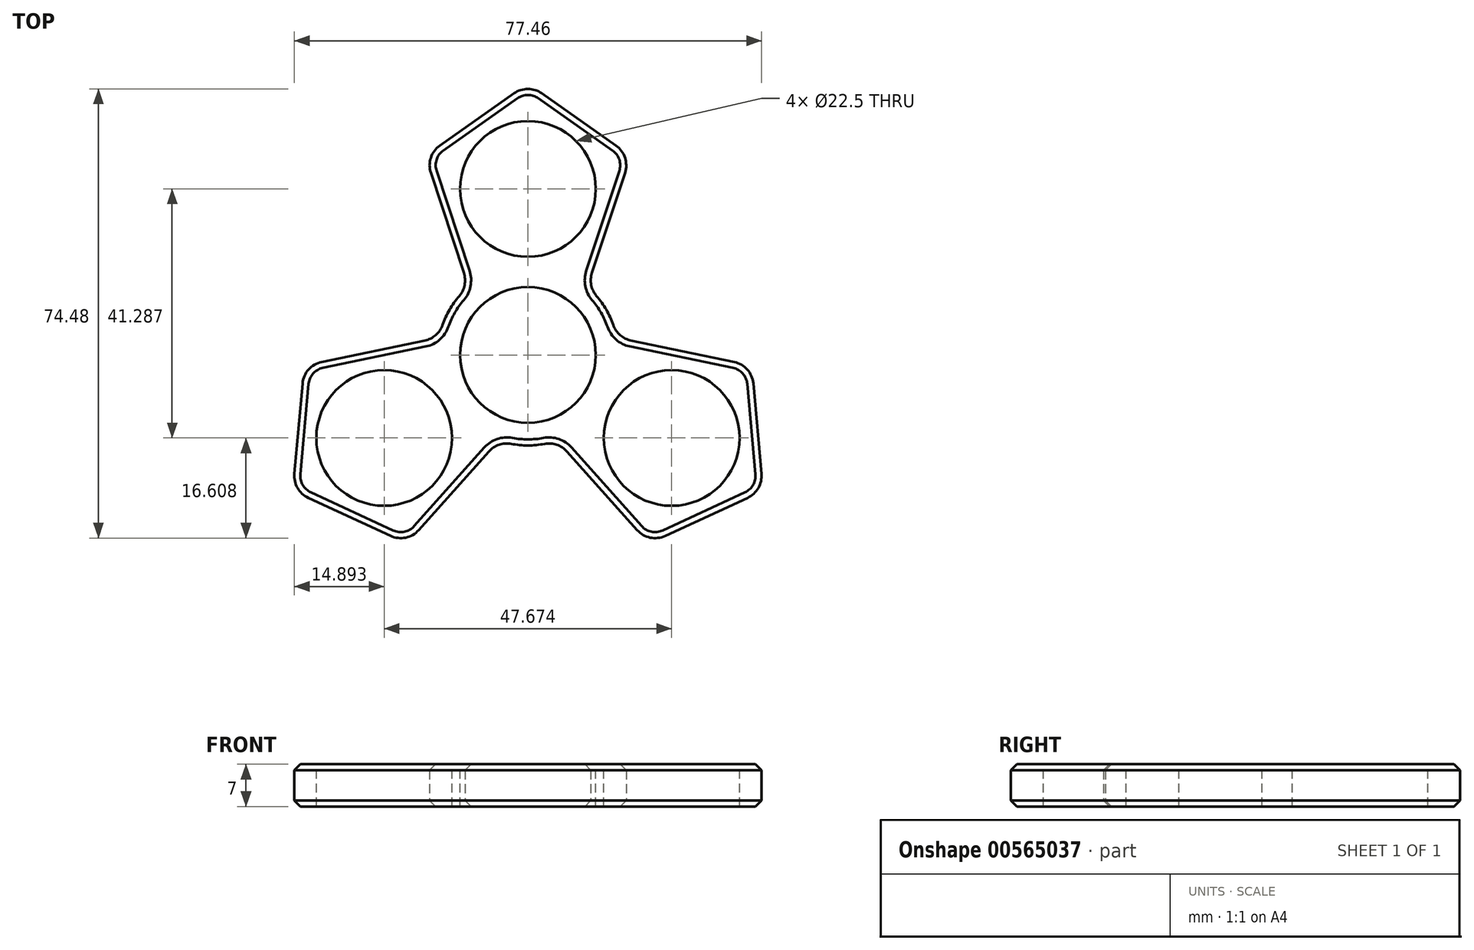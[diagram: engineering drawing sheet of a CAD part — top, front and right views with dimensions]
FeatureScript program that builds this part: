
annotation { "Feature Type Name" : "Feature", "Feature Type Description" : "" }
export const myFeature = defineFeature(function(context is Context, id is Id, definition is map)
    precondition{}
    {
        {
            var Q0;
            Q0=qCreatedBy(makeId("Top.planeOp"),FACE);
            var sketch = newSketch(context, id + "F0", { "sketchPlane" : qUnion([Q0])});
            skCircle(sketch, "E0", {"center": v(0, 0) * mm, "radius": 4 * mm});
            skCircle(sketch, "E1", {"center": v(0, 0) * mm, "radius": 45 * mm, "construction": true});
            skCircle(sketch, "E2", {"center": v(0, 27.52) * mm, "radius": 4 * mm});
            skLineSegment(sketch, "E3", {"start": v(0, 45) * mm, "end": v(-17.02, 33) * mm});
            skLineSegment(sketch, "E4", {"start": v(-17.02, 33) * mm, "end": v(-9.86, 11.3) * mm});
            skLineSegment(sketch, "E5.MirrorCS", {"start": v(0, 45) * mm, "end": v(17.02, 33) * mm});
            skLineSegment(sketch, "E6.MirrorCS", {"start": v(17.02, 33) * mm, "end": v(9.86, 11.3) * mm});
            skLineSegment(sketch, "E7.1.0", {"start": v(-38.97, -22.5) * mm, "end": v(-20.08, -31.25) * mm});
            skLineSegment(sketch, "E7.1.1", {"start": v(-20.08, -31.25) * mm, "end": v(-4.86, -14.2) * mm});
            skLineSegment(sketch, "E7.1.2", {"start": v(-38.97, -22.5) * mm, "end": v(-37.1, -1.76) * mm});
            skLineSegment(sketch, "E7.1.3", {"start": v(-37.1, -1.76) * mm, "end": v(-14.72, 2.89) * mm});
            skCircle(sketch, "E7.1.5", {"center": v(-23.84, -13.76) * mm, "radius": 4 * mm});
            skLineSegment(sketch, "E7.2.0", {"start": v(38.97, -22.5) * mm, "end": v(37.1, -1.76) * mm});
            skLineSegment(sketch, "E7.2.1", {"start": v(37.1, -1.76) * mm, "end": v(14.72, 2.89) * mm});
            skLineSegment(sketch, "E7.2.2", {"start": v(38.97, -22.5) * mm, "end": v(20.08, -31.25) * mm});
            skLineSegment(sketch, "E7.2.3", {"start": v(20.08, -31.25) * mm, "end": v(4.86, -14.2) * mm});
            skCircle(sketch, "E7.2.5", {"center": v(23.84, -13.76) * mm, "radius": 4 * mm});
            skCircle(sketch, "E8", {"center": v(0, 0) * mm, "radius": 15 * mm});
            skCircle(sketch, "E9", {"center": v(23.84, -13.76) * mm, "radius": 11.63 * mm});
            skCircle(sketch, "E10.1.1", {"center": v(0, 27.52) * mm, "radius": 11.63 * mm});
            skCircle(sketch, "E10.2.1", {"center": v(-23.84, -13.76) * mm, "radius": 11.63 * mm});
            skCircle(sketch, "E11", {"center": v(0, 0) * mm, "radius": 11.32 * mm});
            skSolve(sketch);
        }
        {
            var Q0;
            Q0 = qSketchRegion(id + "F0", true);
            extrude(context, id + "F1", {"entities" : qUnion([Q0]), "depth" : 7 * mm, "offsetDistance" : 25 * mm});
        }
        {
            var Q0;
            Q0=makeQuery(id+"F1.opExtrude","SWEPT_EDGE",EDGE,{"disambiguationData":[OSD([sQuery(id+"F0.wireOp",EDGE,"E7.1.0"),sQuery(id+"F0.wireOp",EDGE,"E7.1.1")])]});
            var Q1;
            Q1=makeQuery(id+"F1.opExtrude","SWEPT_EDGE",EDGE,{"disambiguationData":[OSD([sQuery(id+"F0.wireOp",EDGE,"E7.2.2"),sQuery(id+"F0.wireOp",EDGE,"E7.2.3")])]});
            var Q2;
            Q2=makeQuery(id+"F1.opExtrude","SWEPT_EDGE",EDGE,{"disambiguationData":[OSD([sQuery(id+"F0.wireOp",EDGE,"E7.2.0"),sQuery(id+"F0.wireOp",EDGE,"E7.2.2")])]});
            var Q3;
            Q3=makeQuery(id+"F1.opExtrude","SWEPT_EDGE",EDGE,{"disambiguationData":[OSD([sQuery(id+"F0.wireOp",EDGE,"E7.2.0"),sQuery(id+"F0.wireOp",EDGE,"E7.2.1")])]});
            var Q4;
            Q4=makeQuery(id+"F1.opExtrude","SWEPT_EDGE",EDGE,{"disambiguationData":[OSD([sQuery(id+"F0.wireOp",EDGE,"E7.2.1"),sQuery(id+"F0.wireOp",EDGE,"E8")])]});
            var Q5;
            Q5=makeQuery(id+"F1.opExtrude","SWEPT_EDGE",EDGE,{"disambiguationData":[OSD([sQuery(id+"F0.wireOp",EDGE,"E6.MirrorCS"),sQuery(id+"F0.wireOp",EDGE,"E8")])]});
            var Q6;
            Q6=makeQuery(id+"F1.opExtrude","SWEPT_EDGE",EDGE,{"disambiguationData":[OSD([sQuery(id+"F0.wireOp",EDGE,"E5.MirrorCS"),sQuery(id+"F0.wireOp",EDGE,"E6.MirrorCS")])]});
            var Q7;
            Q7=makeQuery(id+"F1.opExtrude","SWEPT_EDGE",EDGE,{"disambiguationData":[OSD([sQuery(id+"F0.wireOp",EDGE,"E3"),sQuery(id+"F0.wireOp",EDGE,"E5.MirrorCS")])]});
            var Q8;
            Q8=makeQuery(id+"F1.opExtrude","SWEPT_EDGE",EDGE,{"disambiguationData":[OSD([sQuery(id+"F0.wireOp",EDGE,"E3"),sQuery(id+"F0.wireOp",EDGE,"E4")])]});
            var Q9;
            Q9=makeQuery(id+"F1.opExtrude","SWEPT_EDGE",EDGE,{"disambiguationData":[OSD([sQuery(id+"F0.wireOp",EDGE,"E4"),sQuery(id+"F0.wireOp",EDGE,"E8")])]});
            var Q10;
            Q10=makeQuery(id+"F1.opExtrude","SWEPT_EDGE",EDGE,{"disambiguationData":[OSD([sQuery(id+"F0.wireOp",EDGE,"E7.1.3"),sQuery(id+"F0.wireOp",EDGE,"E8")])]});
            var Q11;
            Q11=makeQuery(id+"F1.opExtrude","SWEPT_EDGE",EDGE,{"disambiguationData":[OSD([sQuery(id+"F0.wireOp",EDGE,"E7.1.2"),sQuery(id+"F0.wireOp",EDGE,"E7.1.3")])]});
            var Q12;
            Q12=makeQuery(id+"F1.opExtrude","SWEPT_EDGE",EDGE,{"disambiguationData":[OSD([sQuery(id+"F0.wireOp",EDGE,"E7.1.0"),sQuery(id+"F0.wireOp",EDGE,"E7.1.2")])]});
            var Q13;
            Q13=makeQuery(id+"F1.opExtrude","SWEPT_EDGE",EDGE,{"disambiguationData":[OSD([sQuery(id+"F0.wireOp",EDGE,"E7.1.1"),sQuery(id+"F0.wireOp",EDGE,"E8")])]});
            var Q14;
            Q14=makeQuery(id+"F1.opExtrude","SWEPT_EDGE",EDGE,{"disambiguationData":[OSD([sQuery(id+"F0.wireOp",EDGE,"E7.2.3"),sQuery(id+"F0.wireOp",EDGE,"E8")])]});
            fillet(context, id + "F2", {"entities" : qUnion([Q0, Q1, Q2, Q3, Q4, Q5, Q6, Q7, Q8, Q9, Q10, Q11, Q12, Q13, Q14]), "radius" : 4 * mm, "tangentPropagation" : true, "allowEdgeOverflow" : false});
        }
        {
            var Q0;
            Q0=makeQuery(id+"F1.opExtrude","CAP_EDGE",EDGE,{"disambiguationData":[OSD([sQuery(id+"F0.wireOp",EDGE,"E4")])],"isStart":false});
            var Q1;
            Q1=makeQuery(id+"F1.opExtrude","CAP_EDGE",EDGE,{"disambiguationData":[OSD([sQuery(id+"F0.wireOp",EDGE,"E4")])],"isStart":true});
            chamfer(context, id + "F3", {"entities" : qUnion([Q0, Q1]), "width" : 1 * mm, "tangentPropagation" : true});
        }
        {
            var Q0;
            Q0=makeQuery(id+"F1.opExtrude","CAP_FACE",FACE,{"disambiguationData":[OSD([sQuery(id+"F0.wireOp",EDGE,"E3"),sQuery(id+"F0.wireOp",EDGE,"E4"),sQuery(id+"F0.wireOp",EDGE,"E5.MirrorCS"),sQuery(id+"F0.wireOp",EDGE,"E6.MirrorCS"),sQuery(id+"F0.wireOp",EDGE,"E7.1.0"),sQuery(id+"F0.wireOp",EDGE,"E7.1.1"),sQuery(id+"F0.wireOp",EDGE,"E7.1.2"),sQuery(id+"F0.wireOp",EDGE,"E7.1.3"),sQuery(id+"F0.wireOp",EDGE,"E7.2.0"),sQuery(id+"F0.wireOp",EDGE,"E7.2.1"),sQuery(id+"F0.wireOp",EDGE,"E7.2.2"),sQuery(id+"F0.wireOp",EDGE,"E7.2.3"),sQuery(id+"F0.wireOp",EDGE,"E8"),sQuery(id+"F0.wireOp",EDGE,"E9"),sQuery(id+"F0.wireOp",EDGE,"E10.1.1"),sQuery(id+"F0.wireOp",EDGE,"E10.2.1"),sQuery(id+"F0.wireOp",EDGE,"E11")])],"isStart":false});
            var sketch = newSketch(context, id + "F4", { "sketchPlane" : qUnion([Q0])});
            skCircle(sketch, "E12", {"center": v(0, 27.52) * mm, "radius": 11.25 * mm});
            skCircle(sketch, "E13", {"center": v(23.84, -13.76) * mm, "radius": 11.25 * mm});
            skCircle(sketch, "E14", {"center": v(-23.84, -13.76) * mm, "radius": 11.25 * mm});
            skCircle(sketch, "E15", {"center": v(-23.84, -13.76) * mm, "radius": 12.02 * mm});
            skCircle(sketch, "E16", {"center": v(23.84, -13.76) * mm, "radius": 12.02 * mm});
            skCircle(sketch, "E17", {"center": v(0, 27.52) * mm, "radius": 12.13 * mm});
            skCircle(sketch, "E18", {"center": v(0, 0) * mm, "radius": 11.25 * mm});
            skCircle(sketch, "E19", {"center": v(0, 0) * mm, "radius": 12.44 * mm});
            skSolve(sketch);
        }
        {
            var Q0;
            Q0=makeQuery(id+"F4.imprint","IMPRINT",FACE,{"disambiguationData":[TD([[makeQuery(id+"F4.imprint","IMPRINT",EDGE,{"derivedFrom":sQuery(id+"F4.wireOp",EDGE,"E18")}),-1.0]])]});
            var Q1;
            Q1=makeQuery(id+"F4.imprint","IMPRINT",FACE,{"disambiguationData":[TD([[makeQuery(id+"F4.imprint","IMPRINT",EDGE,{"derivedFrom":sQuery(id+"F4.wireOp",EDGE,"E12")}),-1.0]])]});
            var Q2;
            Q2=makeQuery(id+"F4.imprint","IMPRINT",FACE,{"disambiguationData":[TD([[makeQuery(id+"F4.imprint","IMPRINT",EDGE,{"derivedFrom":sQuery(id+"F4.wireOp",EDGE,"E14")}),-1.0]])]});
            var Q3;
            Q3=makeQuery(id+"F4.imprint","IMPRINT",FACE,{"disambiguationData":[TD([[makeQuery(id+"F4.imprint","IMPRINT",EDGE,{"derivedFrom":sQuery(id+"F4.wireOp",EDGE,"E13")}),-1.0]])]});
            extrude(context, id + "F5", {"entities" : qUnion([Q0, Q1, Q2, Q3]), "operationType" : NewBodyOperationType.ADD, "oppositeDirection" : true, "depth" : 7 * mm, "offsetDistance" : 25 * mm});
        }
    });
